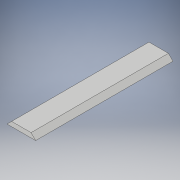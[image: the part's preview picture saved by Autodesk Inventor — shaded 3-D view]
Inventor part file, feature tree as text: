
AUTODESK INVENTOR PART (.ipt)
format: ipt  version: 2019 (Build 230136000, 136)  size: 94,720 bytes
history: native  units: mm
features: extrude x1, sketch x1
ambient origin geometry x8: Origin, YZ Plane, XZ Plane, XY Plane, X Axis, Y Axis, Z Axis, Center Point
bodies: Solide1 (feature_tree)
feature tree (2):
  extrude  "Extrusion1"  Depth=50.0mm
  sketch  "Esquisse1"
